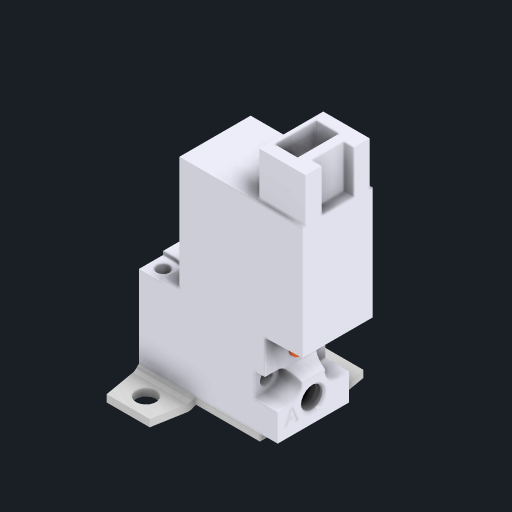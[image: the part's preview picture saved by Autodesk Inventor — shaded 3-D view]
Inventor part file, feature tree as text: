
AUTODESK INVENTOR PART (.ipt)
format: ipt  version: 2023 (Build 270158030, 158C)  size: 373,760 bytes
history: native  units: in
note: dims shown in document units (in); Inventor stores cm internally (conversion verified against a paired STEP export)
features: other x6, thread x3
ambient origin geometry x8: Origin, YZ Plane, XZ Plane, XY Plane, X Axis, Y Axis, Z Axis, Center Point
bodies: Solid1 (feature_tree)
feature tree (9):
  other  "Solenoid, On-Off.iam"
  other  "SY113-SMO-PM3-F.step_1115coil_MDC.ipt:1"
  other  "SY113-SMO-PM3-F.step_MAN-OPA_P.ipt:1"
  other  "Valve Base.ipt:1"
  other  "Bracket.ipt:1"
  other  "Solenoid, On-Off.iam_Bodies"
  thread  "Thread1"  [1 undecoded]
  thread  "Thread2"  [1 undecoded]
  thread  "Thread3"  [1 undecoded]
note: 3 required parameter values undecoded (feature->parameter linkage not recoverable at this tier; creation-order binding heuristic only, values carry confidence <= 0.55)
